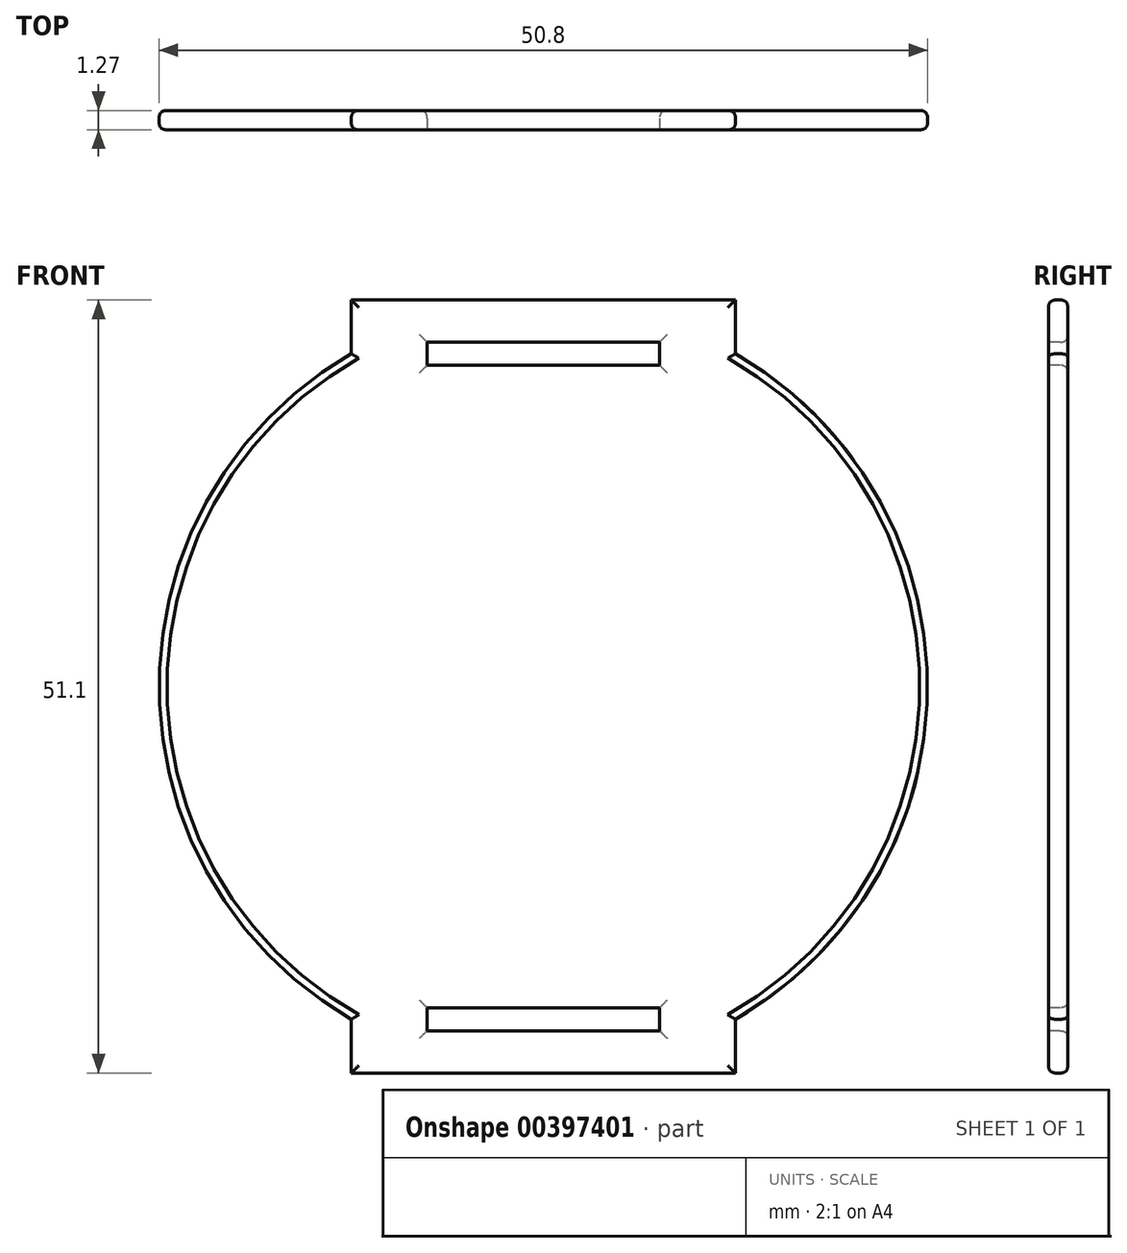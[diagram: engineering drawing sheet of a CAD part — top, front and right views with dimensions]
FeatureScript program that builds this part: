
annotation { "Feature Type Name" : "Feature", "Feature Type Description" : "" }
export const myFeature = defineFeature(function(context is Context, id is Id, definition is map)
    precondition{}
    {
        {
            var Q0;
            Q0=qCreatedBy(makeId("Front.planeOp"),FACE);
            var sketch = newSketch(context, id + "F0", { "sketchPlane" : qUnion([Q0])});
            skArc(sketch, "E0", {"start": v(-12.7, 22) * mm, "mid": v(-25.4, 0) * mm, "end": v(-12.7, -22) * mm});
            skLineSegment(sketch, "E1", {"start": v(-25.4, 0) * mm, "end": v(25.4, 0) * mm});
            skLineSegment(sketch, "E2", {"start": v(-12.7, 22) * mm, "end": v(12.7, 22) * mm});
            skLineSegment(sketch, "E3.MirrorCS", {"start": v(-12.7, -22) * mm, "end": v(12.7, -22) * mm});
            skArc(sketch, "E4.trimOffspring", {"start": v(12.7, -22) * mm, "mid": v(25.4, 0) * mm, "end": v(12.7, 22) * mm});
            skLineSegment(sketch, "E5.top", {"start": v(-12.7, 25.55) * mm, "end": v(12.7, 25.55) * mm});
            skLineSegment(sketch, "E5.left", {"start": v(-12.7, 22) * mm, "end": v(-12.7, 25.55) * mm});
            skLineSegment(sketch, "E5.right", {"start": v(12.7, 22) * mm, "end": v(12.7, 25.55) * mm});
            skLineSegment(sketch, "E6.MirrorCS", {"start": v(-12.7, -22) * mm, "end": v(-12.7, -25.55) * mm});
            skLineSegment(sketch, "E7.MirrorCS", {"start": v(-12.7, -25.55) * mm, "end": v(12.7, -25.55) * mm});
            skLineSegment(sketch, "E8.MirrorCS", {"start": v(12.7, -22) * mm, "end": v(12.7, -25.55) * mm});
            skSolve(sketch);
        }
        {
            var Q0;
            Q0=makeQuery(id+"F0.imprint","IMPRINT",FACE,{"disambiguationData":[TD([[makeQuery(id+"F0.imprint","IMPRINT",EDGE,{"derivedFrom":sQuery(id+"F0.wireOp",EDGE,"E2")}),1.0]])]});
            var Q1;
            {var subQ2=sQuery(id+"F0.wireOp",EDGE,"E1");Q1=makeQuery(id+"F0.imprint","IMPRINT",FACE,{"disambiguationData":[TD([[makeQuery(id+"F0.imprint","IMPRINT",EDGE,{"derivedFrom":subQ2}),1.0]])]});}
            var Q2;
            {var subQ2=sQuery(id+"F0.wireOp",EDGE,"E1");Q2=makeQuery(id+"F0.imprint","IMPRINT",FACE,{"disambiguationData":[TD([[makeQuery(id+"F0.imprint","IMPRINT",EDGE,{"derivedFrom":subQ2}),-1.0]])]});}
            var Q3;
            Q3=makeQuery(id+"F0.imprint","IMPRINT",FACE,{"disambiguationData":[TD([[makeQuery(id+"F0.imprint","IMPRINT",EDGE,{"derivedFrom":sQuery(id+"F0.wireOp",EDGE,"E3.MirrorCS")}),-1.0]])]});
            extrude(context, id + "F1", {"entities" : qUnion([Q0, Q1, Q2, Q3]), "depth" : 1.27 * mm});
        }
        {
            var Q0;
            Q0=makeQuery(id+"F1.opExtrude","CAP_FACE",FACE,{"disambiguationData":[OSD([sQuery(id+"F0.wireOp",EDGE,"E0"),sQuery(id+"F0.wireOp",EDGE,"E4.trimOffspring"),sQuery(id+"F0.wireOp",EDGE,"E5.top"),sQuery(id+"F0.wireOp",EDGE,"E5.left"),sQuery(id+"F0.wireOp",EDGE,"E5.right"),sQuery(id+"F0.wireOp",EDGE,"E6.MirrorCS"),sQuery(id+"F0.wireOp",EDGE,"E7.MirrorCS"),sQuery(id+"F0.wireOp",EDGE,"E8.MirrorCS")])],"isStart":false});
            var sketch = newSketch(context, id + "F2", { "sketchPlane" : qUnion([Q0])});
            skLineSegment(sketch, "E9", {"start": v(-12.7, 22) * mm, "end": v(12.7, 22) * mm});
            skLineSegment(sketch, "E10.bottom", {"start": v(7.69, 21.24) * mm, "end": v(-7.69, 21.24) * mm});
            skLineSegment(sketch, "E10.top", {"start": v(7.69, 22.76) * mm, "end": v(-7.69, 22.76) * mm});
            skLineSegment(sketch, "E10.left", {"start": v(7.69, 21.24) * mm, "end": v(7.69, 22.76) * mm});
            skLineSegment(sketch, "E10.right", {"start": v(-7.69, 21.24) * mm, "end": v(-7.69, 22.76) * mm});
            skPoint(sketch, "E10.middle", {"position": v(0, 22) * mm});
            skLineSegment(sketch, "E11.MirrorCS", {"start": v(7.69, -22.76) * mm, "end": v(-7.69, -22.76) * mm});
            skLineSegment(sketch, "E12.MirrorCS", {"start": v(-7.69, -21.24) * mm, "end": v(-7.69, -22.76) * mm});
            skLineSegment(sketch, "E13.MirrorCS", {"start": v(7.69, -21.24) * mm, "end": v(-7.69, -21.24) * mm});
            skLineSegment(sketch, "E14.MirrorCS", {"start": v(7.69, -21.24) * mm, "end": v(7.69, -22.76) * mm});
            skSolve(sketch);
        }
        {
            var Q0;
            {var subQ5=sQuery(id+"F2.wireOp",EDGE,"E10.bottom");Q0=makeQuery(id+"F2.imprint","IMPRINT",FACE,{"disambiguationData":[TD([[makeQuery(id+"F2.imprint","IMPRINT",EDGE,{"derivedFrom":subQ5}),-1.0]])]});}
            var Q1;
            {var subQ5=sQuery(id+"F2.wireOp",EDGE,"E10.top");Q1=makeQuery(id+"F2.imprint","IMPRINT",FACE,{"disambiguationData":[TD([[makeQuery(id+"F2.imprint","IMPRINT",EDGE,{"derivedFrom":subQ5}),1.0]])]});}
            var Q2;
            Q2=makeQuery(id+"F2.imprint","IMPRINT",FACE,{"disambiguationData":[TD([[makeQuery(id+"F2.imprint","IMPRINT",EDGE,{"derivedFrom":sQuery(id+"F2.wireOp",EDGE,"E11.MirrorCS")}),-1.0]])]});
            extrude(context, id + "F3", {"entities" : qUnion([Q0, Q1, Q2]), "operationType" : NewBodyOperationType.REMOVE, "endBound" : BoundingType.THROUGH_ALL, "oppositeDirection" : true, "depth" : 25.4 * mm});
        }
        {
            var Q0;
            Q0=makeQuery(id+"F1.opExtrude","CAP_EDGE",EDGE,{"disambiguationData":[OSD([sQuery(id+"F0.wireOp",EDGE,"E4.trimOffspring")])],"isStart":true});
            var Q1;
            Q1=makeQuery(id+"F1.opExtrude","CAP_EDGE",EDGE,{"disambiguationData":[OSD([sQuery(id+"F0.wireOp",EDGE,"E5.right")])],"isStart":true});
            var Q2;
            Q2=makeQuery(id+"F1.opExtrude","CAP_EDGE",EDGE,{"disambiguationData":[OSD([sQuery(id+"F0.wireOp",EDGE,"E5.top")])],"isStart":true});
            var Q3;
            Q3=makeQuery(id+"F1.opExtrude","CAP_EDGE",EDGE,{"disambiguationData":[OSD([sQuery(id+"F0.wireOp",EDGE,"E5.left")])],"isStart":true});
            var Q4;
            Q4=makeQuery(id+"F1.opExtrude","CAP_EDGE",EDGE,{"disambiguationData":[OSD([sQuery(id+"F0.wireOp",EDGE,"E0")])],"isStart":true});
            var Q5;
            Q5=makeQuery(id+"F1.opExtrude","CAP_EDGE",EDGE,{"disambiguationData":[OSD([sQuery(id+"F0.wireOp",EDGE,"E6.MirrorCS")])],"isStart":true});
            var Q6;
            Q6=makeQuery(id+"F1.opExtrude","CAP_EDGE",EDGE,{"disambiguationData":[OSD([sQuery(id+"F0.wireOp",EDGE,"E7.MirrorCS")])],"isStart":true});
            var Q7;
            Q7=makeQuery(id+"F1.opExtrude","CAP_EDGE",EDGE,{"disambiguationData":[OSD([sQuery(id+"F0.wireOp",EDGE,"E8.MirrorCS")])],"isStart":true});
            var Q8;
            Q8=makeQuery(id+"F3.boolean.opBoolean","INTERSECT",EDGE,{"derivedFrom":[makeQuery(id+"F1.opExtrude","CAP_FACE",FACE,{"disambiguationData":[OSD([sQuery(id+"F0.wireOp",EDGE,"E0"),sQuery(id+"F0.wireOp",EDGE,"E4.trimOffspring"),sQuery(id+"F0.wireOp",EDGE,"E5.top"),sQuery(id+"F0.wireOp",EDGE,"E5.left"),sQuery(id+"F0.wireOp",EDGE,"E5.right"),sQuery(id+"F0.wireOp",EDGE,"E6.MirrorCS"),sQuery(id+"F0.wireOp",EDGE,"E7.MirrorCS"),sQuery(id+"F0.wireOp",EDGE,"E8.MirrorCS")])],"isStart":true}),makeQuery(id+"F3.opExtrude","SWEPT_FACE",FACE,{"disambiguationData":[OSD([sQuery(id+"F2.wireOp",EDGE,"E14.MirrorCS")])]})]});
            var Q9;
            Q9=makeQuery(id+"F3.boolean.opBoolean","INTERSECT",EDGE,{"derivedFrom":[makeQuery(id+"F1.opExtrude","CAP_FACE",FACE,{"disambiguationData":[OSD([sQuery(id+"F0.wireOp",EDGE,"E0"),sQuery(id+"F0.wireOp",EDGE,"E4.trimOffspring"),sQuery(id+"F0.wireOp",EDGE,"E5.top"),sQuery(id+"F0.wireOp",EDGE,"E5.left"),sQuery(id+"F0.wireOp",EDGE,"E5.right"),sQuery(id+"F0.wireOp",EDGE,"E6.MirrorCS"),sQuery(id+"F0.wireOp",EDGE,"E7.MirrorCS"),sQuery(id+"F0.wireOp",EDGE,"E8.MirrorCS")])],"isStart":true}),makeQuery(id+"F3.opExtrude","SWEPT_FACE",FACE,{"disambiguationData":[OSD([sQuery(id+"F2.wireOp",EDGE,"E13.MirrorCS")])]})]});
            var Q10;
            Q10=makeQuery(id+"F3.boolean.opBoolean","INTERSECT",EDGE,{"derivedFrom":[makeQuery(id+"F1.opExtrude","CAP_FACE",FACE,{"disambiguationData":[OSD([sQuery(id+"F0.wireOp",EDGE,"E0"),sQuery(id+"F0.wireOp",EDGE,"E4.trimOffspring"),sQuery(id+"F0.wireOp",EDGE,"E5.top"),sQuery(id+"F0.wireOp",EDGE,"E5.left"),sQuery(id+"F0.wireOp",EDGE,"E5.right"),sQuery(id+"F0.wireOp",EDGE,"E6.MirrorCS"),sQuery(id+"F0.wireOp",EDGE,"E7.MirrorCS"),sQuery(id+"F0.wireOp",EDGE,"E8.MirrorCS")])],"isStart":true}),makeQuery(id+"F3.opExtrude","SWEPT_FACE",FACE,{"disambiguationData":[OSD([sQuery(id+"F2.wireOp",EDGE,"E12.MirrorCS")])]})]});
            var Q11;
            Q11=makeQuery(id+"F3.boolean.opBoolean","INTERSECT",EDGE,{"derivedFrom":[makeQuery(id+"F1.opExtrude","CAP_FACE",FACE,{"disambiguationData":[OSD([sQuery(id+"F0.wireOp",EDGE,"E0"),sQuery(id+"F0.wireOp",EDGE,"E4.trimOffspring"),sQuery(id+"F0.wireOp",EDGE,"E5.top"),sQuery(id+"F0.wireOp",EDGE,"E5.left"),sQuery(id+"F0.wireOp",EDGE,"E5.right"),sQuery(id+"F0.wireOp",EDGE,"E6.MirrorCS"),sQuery(id+"F0.wireOp",EDGE,"E7.MirrorCS"),sQuery(id+"F0.wireOp",EDGE,"E8.MirrorCS")])],"isStart":true}),makeQuery(id+"F3.opExtrude","SWEPT_FACE",FACE,{"disambiguationData":[OSD([sQuery(id+"F2.wireOp",EDGE,"E11.MirrorCS")])]})]});
            var Q12;
            Q12=makeQuery(id+"F3.boolean.opBoolean","INTERSECT",EDGE,{"derivedFrom":[makeQuery(id+"F1.opExtrude","CAP_FACE",FACE,{"disambiguationData":[OSD([sQuery(id+"F0.wireOp",EDGE,"E0"),sQuery(id+"F0.wireOp",EDGE,"E4.trimOffspring"),sQuery(id+"F0.wireOp",EDGE,"E5.top"),sQuery(id+"F0.wireOp",EDGE,"E5.left"),sQuery(id+"F0.wireOp",EDGE,"E5.right"),sQuery(id+"F0.wireOp",EDGE,"E6.MirrorCS"),sQuery(id+"F0.wireOp",EDGE,"E7.MirrorCS"),sQuery(id+"F0.wireOp",EDGE,"E8.MirrorCS")])],"isStart":true}),makeQuery(id+"F3.opExtrude","SWEPT_FACE",FACE,{"disambiguationData":[OSD([sQuery(id+"F2.wireOp",EDGE,"E10.top")])]})]});
            var Q13;
            Q13=makeQuery(id+"F3.boolean.opBoolean","INTERSECT",EDGE,{"derivedFrom":[makeQuery(id+"F1.opExtrude","CAP_FACE",FACE,{"disambiguationData":[OSD([sQuery(id+"F0.wireOp",EDGE,"E0"),sQuery(id+"F0.wireOp",EDGE,"E4.trimOffspring"),sQuery(id+"F0.wireOp",EDGE,"E5.top"),sQuery(id+"F0.wireOp",EDGE,"E5.left"),sQuery(id+"F0.wireOp",EDGE,"E5.right"),sQuery(id+"F0.wireOp",EDGE,"E6.MirrorCS"),sQuery(id+"F0.wireOp",EDGE,"E7.MirrorCS"),sQuery(id+"F0.wireOp",EDGE,"E8.MirrorCS")])],"isStart":true}),makeQuery(id+"F3.opExtrude","SWEPT_FACE",FACE,{"disambiguationData":[OSD([sQuery(id+"F2.wireOp",EDGE,"E10.right")])]})]});
            var Q14;
            Q14=makeQuery(id+"F3.boolean.opBoolean","INTERSECT",EDGE,{"derivedFrom":[makeQuery(id+"F1.opExtrude","CAP_FACE",FACE,{"disambiguationData":[OSD([sQuery(id+"F0.wireOp",EDGE,"E0"),sQuery(id+"F0.wireOp",EDGE,"E4.trimOffspring"),sQuery(id+"F0.wireOp",EDGE,"E5.top"),sQuery(id+"F0.wireOp",EDGE,"E5.left"),sQuery(id+"F0.wireOp",EDGE,"E5.right"),sQuery(id+"F0.wireOp",EDGE,"E6.MirrorCS"),sQuery(id+"F0.wireOp",EDGE,"E7.MirrorCS"),sQuery(id+"F0.wireOp",EDGE,"E8.MirrorCS")])],"isStart":true}),makeQuery(id+"F3.opExtrude","SWEPT_FACE",FACE,{"disambiguationData":[OSD([sQuery(id+"F2.wireOp",EDGE,"E10.bottom")])]})]});
            var Q15;
            Q15=makeQuery(id+"F3.boolean.opBoolean","INTERSECT",EDGE,{"derivedFrom":[makeQuery(id+"F1.opExtrude","CAP_FACE",FACE,{"disambiguationData":[OSD([sQuery(id+"F0.wireOp",EDGE,"E0"),sQuery(id+"F0.wireOp",EDGE,"E4.trimOffspring"),sQuery(id+"F0.wireOp",EDGE,"E5.top"),sQuery(id+"F0.wireOp",EDGE,"E5.left"),sQuery(id+"F0.wireOp",EDGE,"E5.right"),sQuery(id+"F0.wireOp",EDGE,"E6.MirrorCS"),sQuery(id+"F0.wireOp",EDGE,"E7.MirrorCS"),sQuery(id+"F0.wireOp",EDGE,"E8.MirrorCS")])],"isStart":true}),makeQuery(id+"F3.opExtrude","SWEPT_FACE",FACE,{"disambiguationData":[OSD([sQuery(id+"F2.wireOp",EDGE,"E10.left")])]})]});
            var Q16;
            Q16=makeQuery(id+"F1.opExtrude","CAP_EDGE",EDGE,{"disambiguationData":[OSD([sQuery(id+"F0.wireOp",EDGE,"E0")])],"isStart":false});
            var Q17;
            Q17=makeQuery(id+"F1.opExtrude","CAP_EDGE",EDGE,{"disambiguationData":[OSD([sQuery(id+"F0.wireOp",EDGE,"E6.MirrorCS")])],"isStart":false});
            var Q18;
            Q18=makeQuery(id+"F1.opExtrude","CAP_EDGE",EDGE,{"disambiguationData":[OSD([sQuery(id+"F0.wireOp",EDGE,"E7.MirrorCS")])],"isStart":false});
            var Q19;
            Q19=makeQuery(id+"F1.opExtrude","CAP_EDGE",EDGE,{"disambiguationData":[OSD([sQuery(id+"F0.wireOp",EDGE,"E8.MirrorCS")])],"isStart":false});
            var Q20;
            Q20=makeQuery(id+"F1.opExtrude","CAP_EDGE",EDGE,{"disambiguationData":[OSD([sQuery(id+"F0.wireOp",EDGE,"E4.trimOffspring")])],"isStart":false});
            var Q21;
            Q21=makeQuery(id+"F1.opExtrude","CAP_EDGE",EDGE,{"disambiguationData":[OSD([sQuery(id+"F0.wireOp",EDGE,"E5.left")])],"isStart":false});
            var Q22;
            Q22=makeQuery(id+"F1.opExtrude","CAP_EDGE",EDGE,{"disambiguationData":[OSD([sQuery(id+"F0.wireOp",EDGE,"E5.top")])],"isStart":false});
            var Q23;
            Q23=makeQuery(id+"F1.opExtrude","CAP_EDGE",EDGE,{"disambiguationData":[OSD([sQuery(id+"F0.wireOp",EDGE,"E5.right")])],"isStart":false});
            var Q24;
            Q24=makeQuery(id+"F3.boolean.opBoolean","COPY",EDGE,{"derivedFrom":makeQuery(id+"F3.opExtrude","CAP_EDGE",EDGE,{"disambiguationData":[OSD([sQuery(id+"F2.wireOp",EDGE,"E10.left")])],"isStart":true})});
            var Q25;
            Q25=makeQuery(id+"F3.boolean.opBoolean","COPY",EDGE,{"derivedFrom":makeQuery(id+"F3.opExtrude","CAP_EDGE",EDGE,{"disambiguationData":[OSD([sQuery(id+"F2.wireOp",EDGE,"E10.top")])],"isStart":true})});
            var Q26;
            Q26=makeQuery(id+"F3.boolean.opBoolean","COPY",EDGE,{"derivedFrom":makeQuery(id+"F3.opExtrude","CAP_EDGE",EDGE,{"disambiguationData":[OSD([sQuery(id+"F2.wireOp",EDGE,"E10.bottom")])],"isStart":true})});
            var Q27;
            Q27=makeQuery(id+"F3.boolean.opBoolean","COPY",EDGE,{"derivedFrom":makeQuery(id+"F3.opExtrude","CAP_EDGE",EDGE,{"disambiguationData":[OSD([sQuery(id+"F2.wireOp",EDGE,"E10.right")])],"isStart":true})});
            var Q28;
            Q28=makeQuery(id+"F3.boolean.opBoolean","COPY",EDGE,{"derivedFrom":makeQuery(id+"F3.opExtrude","CAP_EDGE",EDGE,{"disambiguationData":[OSD([sQuery(id+"F2.wireOp",EDGE,"E13.MirrorCS")])],"isStart":true})});
            var Q29;
            Q29=makeQuery(id+"F3.boolean.opBoolean","COPY",EDGE,{"derivedFrom":makeQuery(id+"F3.opExtrude","CAP_EDGE",EDGE,{"disambiguationData":[OSD([sQuery(id+"F2.wireOp",EDGE,"E14.MirrorCS")])],"isStart":true})});
            var Q30;
            Q30=makeQuery(id+"F3.boolean.opBoolean","COPY",EDGE,{"derivedFrom":makeQuery(id+"F3.opExtrude","CAP_EDGE",EDGE,{"disambiguationData":[OSD([sQuery(id+"F2.wireOp",EDGE,"E11.MirrorCS")])],"isStart":true})});
            var Q31;
            Q31=makeQuery(id+"F3.boolean.opBoolean","COPY",EDGE,{"derivedFrom":makeQuery(id+"F3.opExtrude","CAP_EDGE",EDGE,{"disambiguationData":[OSD([sQuery(id+"F2.wireOp",EDGE,"E12.MirrorCS")])],"isStart":true})});
            fillet(context, id + "F4", {"entities" : qUnion([Q0, Q1, Q2, Q3, Q4, Q5, Q6, Q7, Q8, Q9, Q10, Q11, Q12, Q13, Q14, Q15, Q16, Q17, Q18, Q19, Q20, Q21, Q22, Q23, Q24, Q25, Q26, Q27, Q28, Q29, Q30, Q31]), "radius" : 0.5 * mm, "rho" : 0.5, "crossSection" : FilletCrossSection.CONIC, "allowEdgeOverflow" : false});
        }
    });
